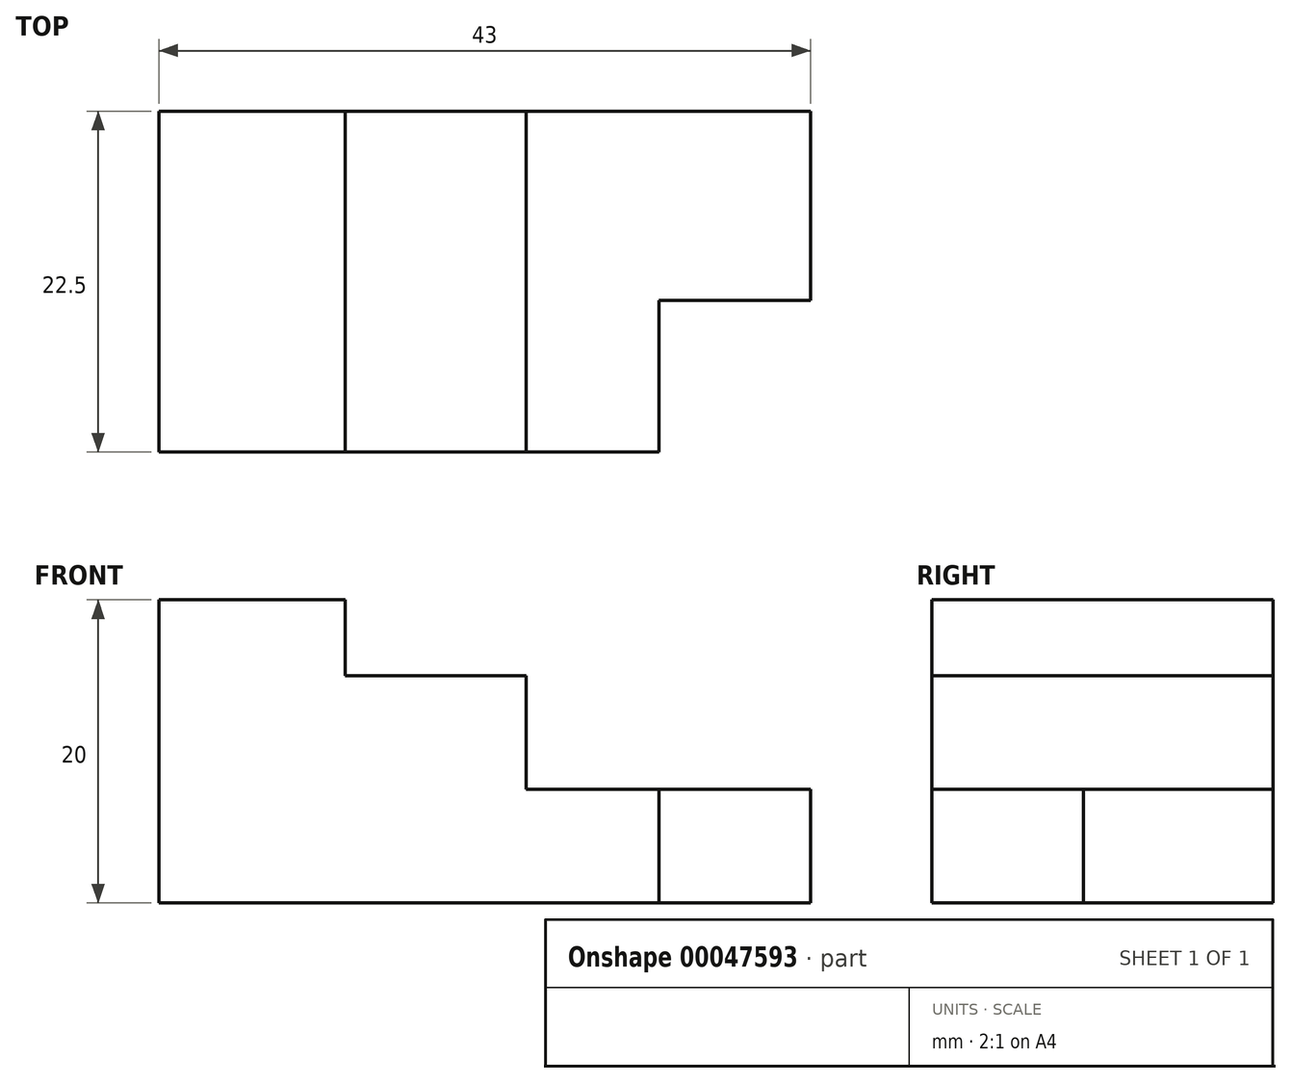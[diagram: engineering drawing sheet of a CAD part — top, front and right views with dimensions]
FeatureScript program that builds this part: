
annotation { "Feature Type Name" : "Feature", "Feature Type Description" : "" }
export const myFeature = defineFeature(function(context is Context, id is Id, definition is map)
    precondition{}
    {
        {
            var Q0;
            Q0=qCreatedBy(makeId("Front.planeOp"),FACE);
            var sketch = newSketch(context, id + "F0", { "sketchPlane" : qUnion([Q0])});
            skLineSegment(sketch, "E0", {"start": v(0, 0) * mm, "end": v(0, 20) * mm});
            skLineSegment(sketch, "E1", {"start": v(0, 20) * mm, "end": v(12.31, 20) * mm});
            skLineSegment(sketch, "E2", {"start": v(12.31, 20) * mm, "end": v(12.31, 15) * mm});
            skLineSegment(sketch, "E3", {"start": v(12.31, 15) * mm, "end": v(24.23, 15) * mm});
            skLineSegment(sketch, "E4", {"start": v(24.23, 15) * mm, "end": v(24.23, 7.5) * mm});
            skLineSegment(sketch, "E5", {"start": v(24.23, 7.5) * mm, "end": v(43, 7.5) * mm});
            skLineSegment(sketch, "E6", {"start": v(43, 7.5) * mm, "end": v(43, 0) * mm});
            skLineSegment(sketch, "E7", {"start": v(43, 0) * mm, "end": v(0, 0) * mm});
            skSolve(sketch);
        }
        {
            var Q0;
            Q0 = qSketchRegion(id + "F0", true);
            extrude(context, id + "F1", {"entities" : qUnion([Q0]), "oppositeDirection" : true, "depth" : 22.5 * mm});
        }
        {
            var Q0;
            Q0=makeQuery(id+"F1.opExtrude","SWEPT_FACE",FACE,{"disambiguationData":[OSD([sQuery(id+"F0.wireOp",EDGE,"E5")])]});
            var sketch = newSketch(context, id + "F2", { "sketchPlane" : qUnion([Q0])});
            skLineSegment(sketch, "E8.bottom", {"start": v(43, 0) * mm, "end": v(33, 0) * mm});
            skLineSegment(sketch, "E8.top", {"start": v(43, 10) * mm, "end": v(33, 10) * mm});
            skLineSegment(sketch, "E8.left", {"start": v(43, 0) * mm, "end": v(43, 10) * mm});
            skLineSegment(sketch, "E8.right", {"start": v(33, 0) * mm, "end": v(33, 10) * mm});
            skSolve(sketch);
        }
        {
            var Q0;
            Q0 = qSketchRegion(id + "F2", true);
            extrude(context, id + "F3", {"entities" : qUnion([Q0]), "operationType" : NewBodyOperationType.REMOVE, "oppositeDirection" : true, "depth" : 25 * mm});
        }
    });
